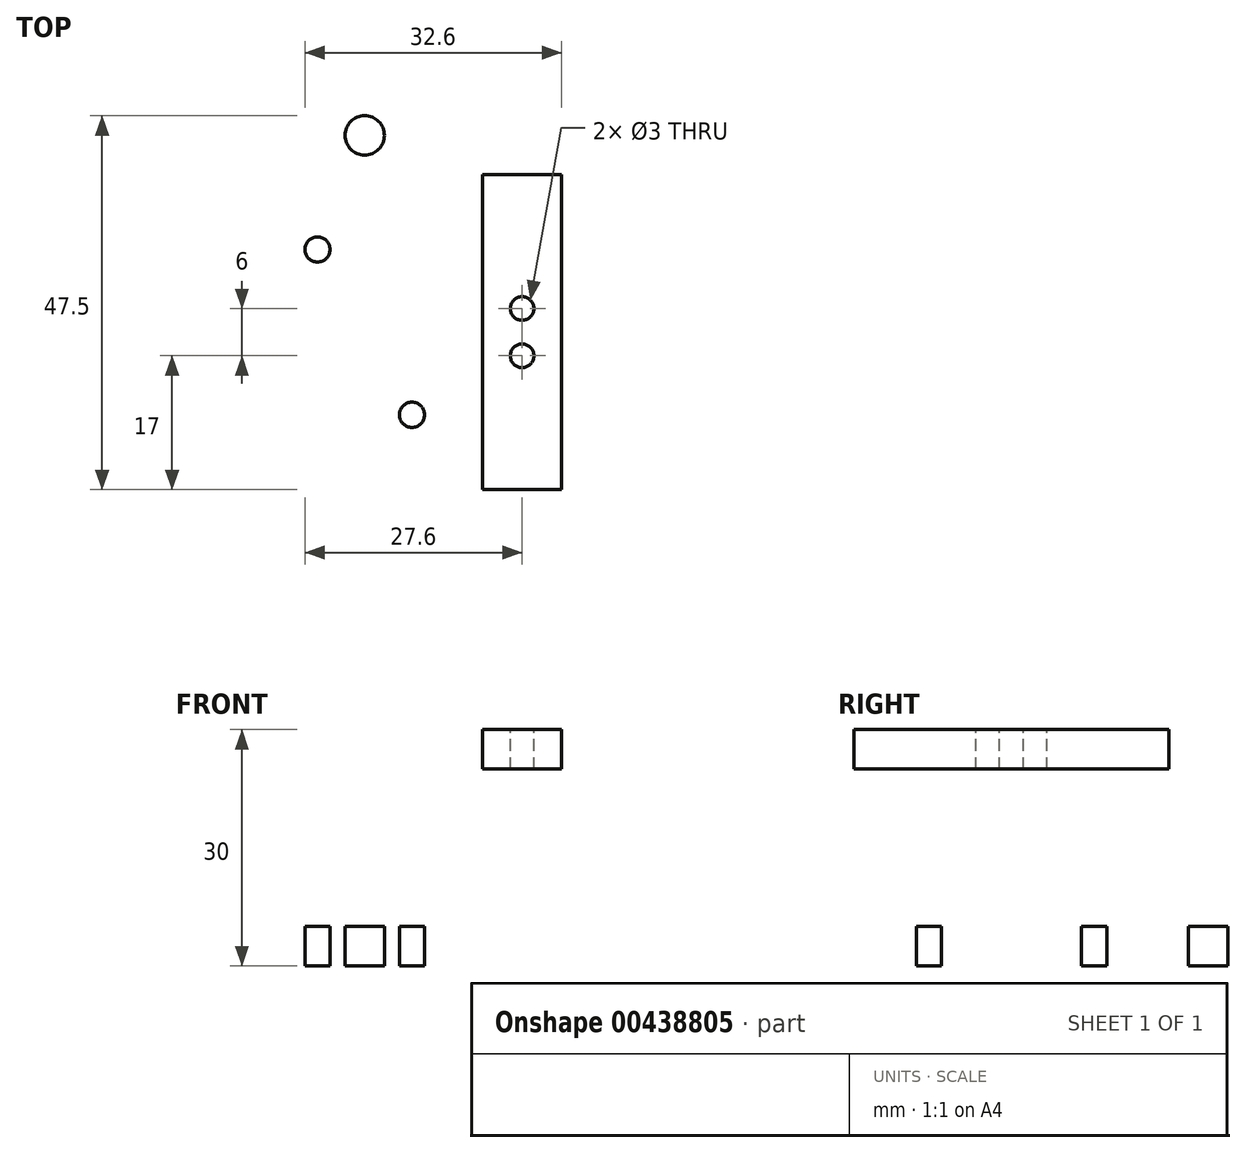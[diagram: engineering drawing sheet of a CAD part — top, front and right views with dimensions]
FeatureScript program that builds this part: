
annotation { "Feature Type Name" : "Feature", "Feature Type Description" : "" }
export const myFeature = defineFeature(function(context is Context, id is Id, definition is map)
    precondition{}
    {
        {
            var Q0;
            Q0=qCreatedBy(makeId("Front.planeOp"),FACE);
            var sketch = newSketch(context, id + "F0", { "sketchPlane" : qUnion([Q0])});
            skLineSegment(sketch, "E0.bottom", {"start": v(25, -15) * mm, "end": v(-15, -15) * mm});
            skLineSegment(sketch, "E0.top", {"start": v(25, 15) * mm, "end": v(15, 15) * mm});
            skLineSegment(sketch, "E0.left", {"start": v(25, -15) * mm, "end": v(25, 15) * mm});
            skPoint(sketch, "E0.middle", {"position": v(0, 0) * mm});
            skLineSegment(sketch, "E1.MirrorCS", {"start": v(15, 15) * mm, "end": v(15, -10) * mm});
            skLineSegment(sketch, "E2", {"start": v(-15, -10) * mm, "end": v(15, -10) * mm});
            skLineSegment(sketch, "E3", {"start": v(-5, -10) * mm, "end": v(-5, -15) * mm});
            skLineSegment(sketch, "E4.MirrorCS", {"start": v(5, -10) * mm, "end": v(5, -15) * mm});
            skLineSegment(sketch, "E5", {"start": v(-15, -10) * mm, "end": v(-15, -15) * mm});
            skSolve(sketch);
        }
        {
            var Q0;
            Q0 = qSketchRegion(id + "F0", true);
            extrude(context, id + "F1", {"entities" : qUnion([Q0]), "depth" : 40 * mm, "offsetDistance" : 25 * mm, "symmetric" : true});
        }
        {
            var Q0;
            {var subQ0=sQuery(id+"F0.wireOp",EDGE,"E3");Q0=makeQuery(id+"F0.imprint","IMPRINT",FACE,{"disambiguationData":[TD([[makeQuery(id+"F0.imprint","IMPRINT",EDGE,{"derivedFrom":subQ0}),1.0]])]});}
            extrude(context, id + "F2", {"entities" : qUnion([Q0]), "operationType" : NewBodyOperationType.ADD, "depth" : 60 * mm, "offsetDistance" : 25 * mm, "symmetric" : true});
        }
        {
            var Q0;
            {var subQ0=sQuery(id+"F0.wireOp",EDGE,"E0.bottom");Q0=makeQuery(id+"F2.boolean.opBoolean","MERGE",FACE,{"derivedFrom":[makeQuery(id+"F1.opExtrude","SWEPT_FACE",FACE,{"disambiguationData":[OSD([subQ0])]}),makeQuery(id+"F2.opExtrude","SWEPT_FACE",FACE,{"disambiguationData":[OSD([subQ0])]})]});}
            var sketch = newSketch(context, id + "F3", { "sketchPlane" : qUnion([Q0])});
            skCircle(sketch, "E6", {"center": v(-6, 10.5) * mm, "radius": 1.6 * mm});
            skCircle(sketch, "E7.MirrorC", {"center": v(6, 10.5) * mm, "radius": 1.6 * mm});
            skCircle(sketch, "E8.MirrorC", {"center": v(-6, -10.5) * mm, "radius": 1.6 * mm});
            skCircle(sketch, "E9.MirrorC", {"center": v(6, -10.5) * mm, "radius": 1.6 * mm});
            skCircle(sketch, "E10", {"center": v(0, 25) * mm, "radius": 2.5 * mm});
            skCircle(sketch, "E11.MirrorC", {"center": v(0, -25) * mm, "radius": 2.5 * mm});
            skSolve(sketch);
        }
        {
            var Q0;
            Q0=makeQuery(id+"F3.imprint","IMPRINT",FACE,{"disambiguationData":[TD([[makeQuery(id+"F3.imprint","IMPRINT",EDGE,{"derivedFrom":sQuery(id+"F3.wireOp",EDGE,"E10")}),1.0]])]});
            var Q1;
            Q1=makeQuery(id+"F3.imprint","IMPRINT",FACE,{"disambiguationData":[TD([[makeQuery(id+"F3.imprint","IMPRINT",EDGE,{"derivedFrom":sQuery(id+"F3.wireOp",EDGE,"E6")}),1.0]])]});
            var Q2;
            Q2=makeQuery(id+"F3.imprint","IMPRINT",FACE,{"disambiguationData":[TD([[makeQuery(id+"F3.imprint","IMPRINT",EDGE,{"derivedFrom":sQuery(id+"F3.wireOp",EDGE,"E7.MirrorC")}),-1.0]])]});
            var Q3;
            Q3=makeQuery(id+"F3.imprint","IMPRINT",FACE,{"disambiguationData":[TD([[makeQuery(id+"F3.imprint","IMPRINT",EDGE,{"derivedFrom":sQuery(id+"F3.wireOp",EDGE,"E9.MirrorC")}),1.0]])]});
            var Q4;
            Q4=makeQuery(id+"F3.imprint","IMPRINT",FACE,{"disambiguationData":[TD([[makeQuery(id+"F3.imprint","IMPRINT",EDGE,{"derivedFrom":sQuery(id+"F3.wireOp",EDGE,"E8.MirrorC")}),-1.0]])]});
            var Q5;
            Q5=makeQuery(id+"F3.imprint","IMPRINT",FACE,{"disambiguationData":[TD([[makeQuery(id+"F3.imprint","IMPRINT",EDGE,{"derivedFrom":sQuery(id+"F3.wireOp",EDGE,"E11.MirrorC")}),-1.0]])]});
            extrude(context, id + "F4", {"entities" : qUnion([Q0, Q1, Q2, Q3, Q4, Q5]), "operationType" : NewBodyOperationType.REMOVE, "oppositeDirection" : true, "depth" : 25 * mm, "offsetDistance" : 25 * mm});
        }
        {
            var Q0;
            Q0=makeQuery(id+"F1.opExtrude","SWEPT_FACE",FACE,{"disambiguationData":[OSD([sQuery(id+"F0.wireOp",EDGE,"E0.left")])]});
            var sketch = newSketch(context, id + "F5", { "sketchPlane" : qUnion([Q0])});
            skCircle(sketch, "E12", {"center": v(0, 5) * mm, "radius": 4 * mm});
            skPoint(sketch, "E12.centerSnap0", {"position": v(0, 15) * mm});
            skSolve(sketch);
        }
        {
            var Q0;
            Q0=makeQuery(id+"F5.imprint","IMPRINT",FACE,{"disambiguationData":[TD([[makeQuery(id+"F5.imprint","IMPRINT",EDGE,{"derivedFrom":sQuery(id+"F5.wireOp",EDGE,"E12")}),1.0]])]});
            extrude(context, id + "F6", {"entities" : qUnion([Q0]), "operationType" : NewBodyOperationType.REMOVE, "oppositeDirection" : true, "depth" : 8 * mm, "offsetDistance" : 25 * mm});
        }
        {
            var Q0;
            {var subQ0=sQuery(id+"F0.wireOp",EDGE,"E0.left");var subQ1=sQuery(id+"F0.wireOp",EDGE,"E0.bottom");var subQ2=sQuery(id+"F0.wireOp",EDGE,"E0.top");var subQ3=sQuery(id+"F0.wireOp",EDGE,"E1.MirrorCS");var subQ4=sQuery(id+"F0.wireOp",EDGE,"E2");Q0=makeQuery(id+"F2.boolean.opBoolean","SPLIT",FACE,{"disambiguationData":[TD([makeQuery(id+"F1.opExtrude","SWEPT_FACE",FACE,{"disambiguationData":[OSD([subQ2])]})])],"derivedFrom":makeQuery(id+"F1.opExtrude","CAP_FACE",FACE,{"disambiguationData":[OSD([subQ1,subQ2,subQ0,subQ3,sQuery(id+"F0.wireOp",EDGE,"3vg3gNb5-5bti-u4H2-HO9b-LQCKHRAT1MqV"),subQ4])],"isStart":false})});}
            var sketch = newSketch(context, id + "F7", { "sketchPlane" : qUnion([Q0])});
            skCircle(sketch, "E13", {"center": v(20, 6.8) * mm, "radius": 1.5 * mm});
            skSolve(sketch);
        }
        {
            var Q0;
            Q0=makeQuery(id+"F7.imprint","IMPRINT",FACE,{"disambiguationData":[TD([[makeQuery(id+"F7.imprint","IMPRINT",EDGE,{"derivedFrom":sQuery(id+"F7.wireOp",EDGE,"E13")}),1.0]])]});
            extrude(context, id + "F8", {"entities" : qUnion([Q0]), "operationType" : NewBodyOperationType.REMOVE, "oppositeDirection" : true, "depth" : 60 * mm, "offsetDistance" : 25 * mm});
        }
        {
            var Q0;
            Q0=makeQuery(id+"F1.opExtrude","SWEPT_FACE",FACE,{"disambiguationData":[OSD([sQuery(id+"F0.wireOp",EDGE,"E0.top")])]});
            var sketch = newSketch(context, id + "F9", { "sketchPlane" : qUnion([Q0])});
            skCircle(sketch, "E14", {"center": v(20, -3) * mm, "radius": 1.5 * mm});
            skCircle(sketch, "E15.MirrorC", {"center": v(20, 3) * mm, "radius": 1.5 * mm});
            skSolve(sketch);
        }
        {
            var Q0;
            Q0 = qSketchRegion(id + "F9", true);
            extrude(context, id + "F10", {"entities" : qUnion([Q0]), "operationType" : NewBodyOperationType.REMOVE, "oppositeDirection" : true, "depth" : 10 * mm, "offsetDistance" : 25 * mm});
        }
    });
